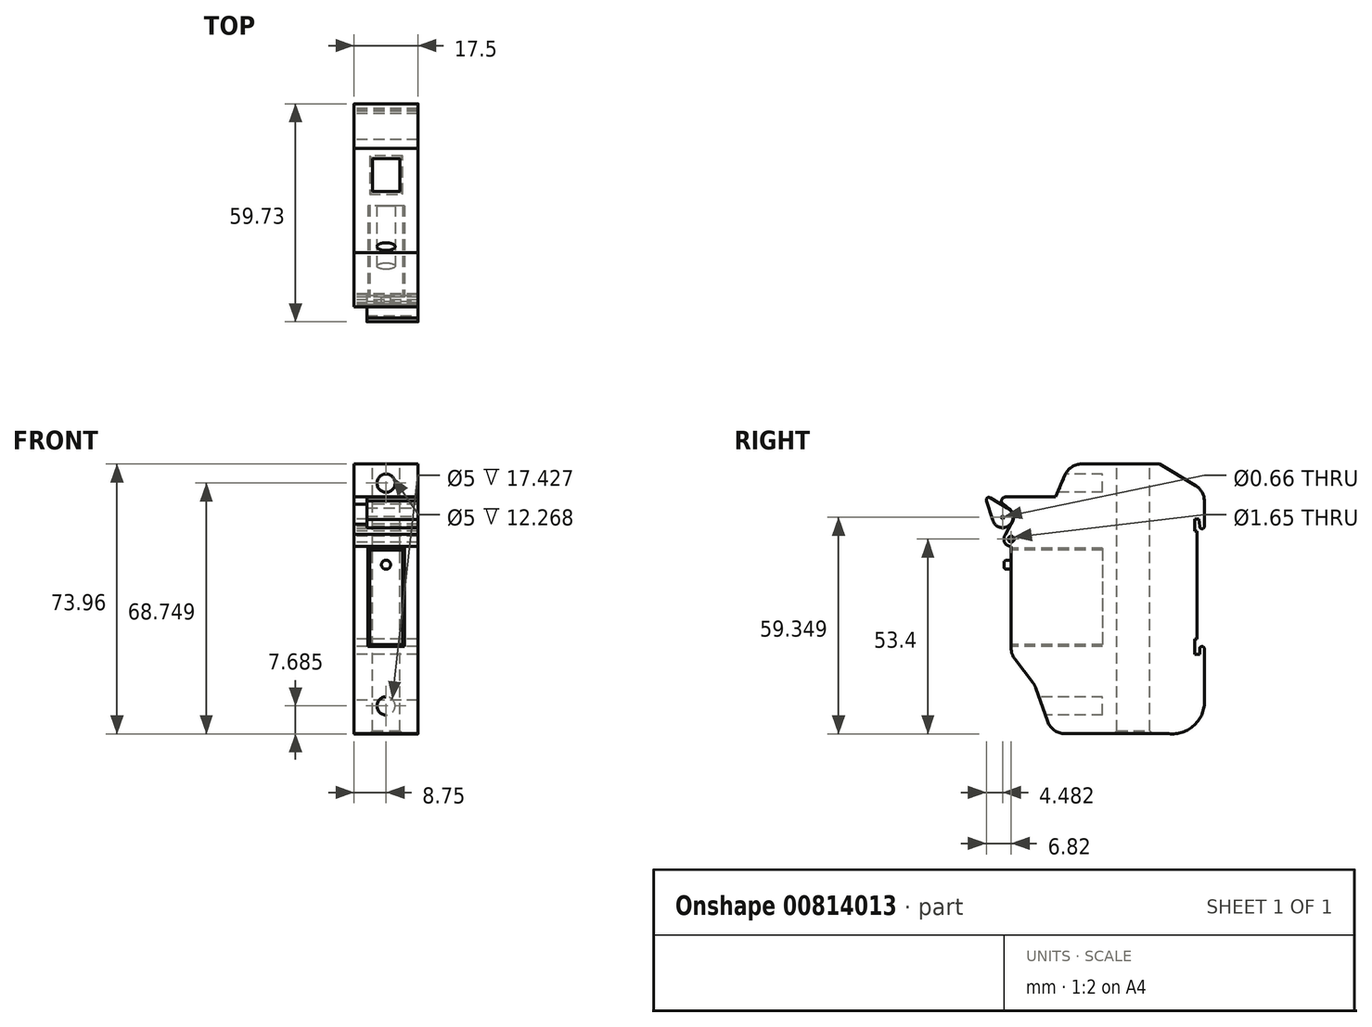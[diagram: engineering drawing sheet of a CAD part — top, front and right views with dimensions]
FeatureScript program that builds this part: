
annotation { "Feature Type Name" : "Feature", "Feature Type Description" : "" }
export const myFeature = defineFeature(function(context is Context, id is Id, definition is map)
    precondition{}
    {
        {
            var Q0;
            Q0=qCreatedBy(makeId("Right.planeOp"),FACE);
            var sketch = newSketch(context, id + "F0", { "sketchPlane" : qUnion([Q0])});
            skLineSegment(sketch, "E0", {"start": v(0, 86.45) * mm, "end": v(0, 33.6) * mm, "construction": true});
            skLineSegment(sketch, "E1", {"start": v(-101.47, 0) * mm, "end": v(113.77, 0) * mm, "construction": true});
            skLineSegment(sketch, "E2", {"start": v(0, 0) * mm, "end": v(0, -40.3) * mm});
            skLineSegment(sketch, "E3", {"start": v(14.7, -40.3) * mm, "end": v(45.1, -40.3) * mm});
            skLineSegment(sketch, "E4", {"start": v(52.9, -32.04) * mm, "end": v(52.9, -17.04) * mm});
            skLineSegment(sketch, "E5", {"start": v(40.66, 33.6) * mm, "end": v(19.3, 33.6) * mm});
            skLineSegment(sketch, "E6.bottom", {"start": v(51.37, 18.6) * mm, "end": v(50.3, 18.6) * mm});
            skLineSegment(sketch, "E6.top", {"start": v(52.9, -18.6) * mm, "end": v(50.3, -18.6) * mm});
            skLineSegment(sketch, "E6.right", {"start": v(50.3, 18.6) * mm, "end": v(50.3, 15.23) * mm});
            skPoint(sketch, "E6.middle", {"position": v(52.9, 0) * mm});
            skLineSegment(sketch, "E7", {"start": v(51.37, 18.6) * mm, "end": v(51.6, 16.51) * mm});
            skLineSegment(sketch, "E8.bottom", {"start": v(50.3, 15.23) * mm, "end": v(50.92, 15.23) * mm});
            skLineSegment(sketch, "E8.top", {"start": v(50.3, -14.35) * mm, "end": v(50.92, -14.35) * mm});
            skLineSegment(sketch, "E8.right", {"start": v(50.92, 15.23) * mm, "end": v(50.92, -14.35) * mm});
            skPoint(sketch, "E9.orphan", {"position": v(55.5, -18.6) * mm});
            skPoint(sketch, "E6.left.start.orphan", {"position": v(55.5, 18.6) * mm});
            skLineSegment(sketch, "E10.trimOffspring", {"start": v(52.9, 16.51) * mm, "end": v(52.9, 23.43) * mm});
            skLineSegment(sketch, "E11", {"start": v(51.6, -18.6) * mm, "end": v(51.6, -17.04) * mm});
            skLineSegment(sketch, "E12", {"start": v(52.9, -17.04) * mm, "end": v(52.9, -18.6) * mm});
            skArc(sketch, "E13", {"start": v(52.9, -17.04) * mm, "mid": v(52.25, -16.4) * mm, "end": v(51.6, -17.04) * mm});
            skArc(sketch, "E14", {"start": v(51.6, 16.51) * mm, "mid": v(52.25, 15.86) * mm, "end": v(52.9, 16.51) * mm});
            skLineSegment(sketch, "E15.trimOffspring", {"start": v(50.3, -14.35) * mm, "end": v(50.3, -18.6) * mm});
            skLineSegment(sketch, "E16", {"start": v(50.47, 27.72) * mm, "end": v(40.66, 33.6) * mm});
            skArc(sketch, "E17", {"start": v(43.12, -40.3) * mm, "mid": v(50.15, -37.96) * mm, "end": v(52.9, -31.07) * mm});
            skLineSegment(sketch, "E18.trimOffspring", {"start": v(0, -40.3) * mm, "end": v(0, -83.55) * mm, "construction": true});
            skLineSegment(sketch, "E19", {"start": v(9.98, -36.97) * mm, "end": v(6.69, -27.67) * mm});
            skLineSegment(sketch, "E20", {"start": v(5.93, -26.28) * mm, "end": v(1.04, -19.95) * mm});
            skLineSegment(sketch, "E21", {"start": v(0, 24.58) * mm, "end": v(12.18, 24.58) * mm});
            skLineSegment(sketch, "E22", {"start": v(12.18, 24.58) * mm, "end": v(14.7, 30.55) * mm});
            skArc(sketch, "E23", {"start": v(0, 17.15) * mm, "mid": v(0.61, 19.37) * mm, "end": v(-0.55, 21.36) * mm});
            skCircle(sketch, "E24", {"center": v(0, 13.04) * mm, "radius": 0.82 * mm});
            skArc(sketch, "E25", {"start": v(-1.54, 14.34) * mm, "mid": v(-1.83, 12.2) * mm, "end": v(0, 11.03) * mm});
            skLineSegment(sketch, "E26", {"start": v(-1.54, 14.34) * mm, "end": v(0.26, 17.53) * mm});
            skArc(sketch, "E27", {"start": v(-1.57, 24.58) * mm, "mid": v(-2.62, 23.78) * mm, "end": v(-2.13, 22.56) * mm});
            skLineSegment(sketch, "E28", {"start": v(0, 24.58) * mm, "end": v(-1.57, 24.58) * mm});
            skLineSegment(sketch, "E29", {"start": v(-2.13, 22.56) * mm, "end": v(-0.55, 21.36) * mm});
            skLineSegment(sketch, "E30.trimOffspring", {"start": v(0, 11.03) * mm, "end": v(0, -16.9) * mm, "construction": true});
            skLineSegment(sketch, "E31.trimOffspring", {"start": v(0, 11.03) * mm, "end": v(0, 0) * mm});
            skLineSegment(sketch, "E32.trimOffspring", {"start": v(0, 17.15) * mm, "end": v(0, 17.08) * mm, "construction": true});
            skLineSegment(sketch, "E33.trimOffspring", {"start": v(0, 17.15) * mm, "end": v(0, 17.08) * mm});
            skPoint(sketch, "E34.visualSharp", {"position": v(0, -18.6) * mm});
            skArc(sketch, "E34.filletArc", {"start": v(0, -16.9) * mm, "mid": v(0.27, -18.5) * mm, "end": v(1.04, -19.95) * mm});
            skPoint(sketch, "E35.visualSharp", {"position": v(6.42, -26.91) * mm});
            skArc(sketch, "E35.filletArc", {"start": v(6.69, -27.67) * mm, "mid": v(6.36, -26.94) * mm, "end": v(5.93, -26.28) * mm});
            skPoint(sketch, "E36.visualSharp", {"position": v(11.16, -40.3) * mm});
            skArc(sketch, "E36.filletArc", {"start": v(9.98, -36.97) * mm, "mid": v(11.8, -39.38) * mm, "end": v(14.7, -40.3) * mm});
            skPoint(sketch, "E37.visualSharp", {"position": v(15.99, 33.6) * mm});
            skArc(sketch, "E37.filletArc", {"start": v(19.3, 33.6) * mm, "mid": v(16.54, 32.77) * mm, "end": v(14.7, 30.55) * mm});
            skPoint(sketch, "E38.visualSharp", {"position": v(52.9, 26.27) * mm});
            skArc(sketch, "E38.filletArc", {"start": v(52.9, 23.43) * mm, "mid": v(52.25, 25.9) * mm, "end": v(50.47, 27.72) * mm});
            skSolve(sketch);
        }
        {
            var Q0;
            Q0=qSketchRegion(id+"F0",true);
            extrude(context, id + "F1", {"entities" : qUnion([Q0]), "depth" : 17.5 * mm, "offsetDistance" : 25 * mm});
        }
        {
            var Q0;
            Q0=makeQuery(id+"F1.opExtrude","CAP_FACE",FACE,{"disambiguationData":[OSD([sQuery(id+"F0.wireOp",EDGE,"E2"),sQuery(id+"F0.wireOp",EDGE,"E3"),sQuery(id+"F0.wireOp",EDGE,"E4"),sQuery(id+"F0.wireOp",EDGE,"E5"),sQuery(id+"F0.wireOp",EDGE,"E6.bottom"),sQuery(id+"F0.wireOp",EDGE,"E6.top"),sQuery(id+"F0.wireOp",EDGE,"E6.right"),sQuery(id+"F0.wireOp",EDGE,"E7"),sQuery(id+"F0.wireOp",EDGE,"E8.bottom"),sQuery(id+"F0.wireOp",EDGE,"E8.top"),sQuery(id+"F0.wireOp",EDGE,"E8.right"),sQuery(id+"F0.wireOp",EDGE,"E10.trimOffspring"),sQuery(id+"F0.wireOp",EDGE,"E11"),sQuery(id+"F0.wireOp",EDGE,"E12"),sQuery(id+"F0.wireOp",EDGE,"E13"),sQuery(id+"F0.wireOp",EDGE,"E14"),sQuery(id+"F0.wireOp",EDGE,"E15.trimOffspring"),sQuery(id+"F0.wireOp",EDGE,"E16"),sQuery(id+"F0.wireOp",EDGE,"E17"),sQuery(id+"F0.wireOp",EDGE,"E19"),sQuery(id+"F0.wireOp",EDGE,"E20"),sQuery(id+"F0.wireOp",EDGE,"E21"),sQuery(id+"F0.wireOp",EDGE,"E22"),sQuery(id+"F0.wireOp",EDGE,"E23"),sQuery(id+"F0.wireOp",EDGE,"E24"),sQuery(id+"F0.wireOp",EDGE,"E25"),sQuery(id+"F0.wireOp",EDGE,"E26"),sQuery(id+"F0.wireOp",EDGE,"E27"),sQuery(id+"F0.wireOp",EDGE,"E28"),sQuery(id+"F0.wireOp",EDGE,"E29"),sQuery(id+"F0.wireOp",EDGE,"E31.trimOffspring"),sQuery(id+"F0.wireOp",EDGE,"E33.trimOffspring"),sQuery(id+"F0.wireOp",EDGE,"E34.filletArc"),sQuery(id+"F0.wireOp",EDGE,"E35.filletArc"),sQuery(id+"F0.wireOp",EDGE,"E36.filletArc"),sQuery(id+"F0.wireOp",EDGE,"E37.filletArc"),sQuery(id+"F0.wireOp",EDGE,"E38.filletArc")])],"isStart":false});
            var sketch = newSketch(context, id + "F2", { "sketchPlane" : qUnion([Q0])});
            skArc(sketch, "E39", {"start": v(-5.1, 18.4) * mm, "mid": v(-0.56, 16.8) * mm, "end": v(-1.2, 21.57) * mm});
            skArc(sketch, "E40", {"start": v(-5.77, 24.34) * mm, "mid": v(-6.6, 24.31) * mm, "end": v(-6.73, 23.5) * mm});
            skLineSegment(sketch, "E41", {"start": v(-6.73, 23.5) * mm, "end": v(-4.92, 17.86) * mm});
            skLineSegment(sketch, "E42", {"start": v(-5.77, 24.34) * mm, "end": v(-1.2, 21.57) * mm});
            skCircle(sketch, "E43", {"center": v(-2.34, 18.99) * mm, "radius": 0.33 * mm});
            skSolve(sketch);
        }
        {
            var Q0;
            Q0=qSketchRegion(id+"F2",true);
            extrude(context, id + "F3", {"entities" : qUnion([Q0]), "oppositeDirection" : true, "depth" : 14 * mm, "offsetDistance" : 25 * mm});
        }
        {
            var Q0;
            Q0=makeQuery(id+"F1.opExtrude","SWEPT_FACE",FACE,{"disambiguationData":[OSD([sQuery(id+"F0.wireOp",EDGE,"E5")])]});
            var sketch = newSketch(context, id + "F4", { "sketchPlane" : qUnion([Q0])});
            skLineSegment(sketch, "E44.bottom", {"start": v(5, 37.9) * mm, "end": v(12.5, 37.9) * mm});
            skLineSegment(sketch, "E44.top", {"start": v(5, 28.9) * mm, "end": v(12.5, 28.9) * mm});
            skLineSegment(sketch, "E44.left", {"start": v(5, 37.9) * mm, "end": v(5, 28.9) * mm});
            skLineSegment(sketch, "E44.right", {"start": v(12.5, 37.9) * mm, "end": v(12.5, 28.9) * mm});
            skPoint(sketch, "E44.middle", {"position": v(8.75, 33.4) * mm});
            skPoint(sketch, "E44.middle.positionSnap0", {"position": v(8.75, 19.3) * mm});
            skPoint(sketch, "E44.centerSnap0", {"position": v(8.75, 19.3) * mm});
            skSolve(sketch);
        }
        {
            var Q0;
            Q0=qSketchRegion(id+"F4",true);
            extrude(context, id + "F5", {"entities" : qUnion([Q0]), "operationType" : NewBodyOperationType.REMOVE, "endBound" : BoundingType.THROUGH_ALL, "oppositeDirection" : true, "depth" : 25 * mm, "offsetDistance" : 25 * mm});
        }
        {
            var Q0;
            Q0=qCreatedBy(makeId("Front.planeOp"),FACE);
            var sketch = newSketch(context, id + "F6", { "sketchPlane" : qUnion([Q0])});
            skLineSegment(sketch, "E45", {"start": v(8.75, -59.1) * mm, "end": v(8.75, 50.81) * mm, "construction": true});
            skCircle(sketch, "E46", {"center": v(8.75, -32.68) * mm, "radius": 2.5 * mm});
            skCircle(sketch, "E47", {"center": v(8.75, 28.39) * mm, "radius": 2.5 * mm});
            skSolve(sketch);
        }
        {
            var Q0;
            Q0=qSketchRegion(id+"F6",true);
            extrude(context, id + "F7", {"entities" : qUnion([Q0]), "operationType" : NewBodyOperationType.REMOVE, "oppositeDirection" : true, "depth" : 25 * mm, "offsetDistance" : 25 * mm});
        }
        {
            var Q0;
            Q0=makeQuery(id+"F1.opExtrude","SWEPT_FACE",FACE,{"disambiguationData":[OSD([sQuery(id+"F0.wireOp",EDGE,"E2"),sQuery(id+"F0.wireOp",EDGE,"E31.trimOffspring")])]});
            var sketch = newSketch(context, id + "F8", { "sketchPlane" : qUnion([Q0])});
            skLineSegment(sketch, "E48.bottom", {"start": v(13.75, 10.57) * mm, "end": v(3.75, 10.57) * mm});
            skLineSegment(sketch, "E48.top", {"start": v(13.75, -16.43) * mm, "end": v(3.75, -16.43) * mm});
            skLineSegment(sketch, "E48.left", {"start": v(13.75, 10.57) * mm, "end": v(13.75, -16.43) * mm});
            skLineSegment(sketch, "E48.right", {"start": v(3.75, 10.57) * mm, "end": v(3.75, -16.43) * mm});
            skPoint(sketch, "E48.middle", {"position": v(8.75, -2.93) * mm});
            skPoint(sketch, "E48.middle.positionSnap0", {"position": v(17.5, -2.93) * mm});
            skPoint(sketch, "E48.middle.positionSnap1", {"position": v(8.75, -16.9) * mm});
            skPoint(sketch, "E48.centerSnap0", {"position": v(17.5, -2.93) * mm});
            skPoint(sketch, "E48.centerSnap1", {"position": v(8.75, -16.9) * mm});
            skLineSegment(sketch, "E49.bottom", {"start": v(13.25, 10.07) * mm, "end": v(4.25, 10.07) * mm});
            skLineSegment(sketch, "E49.top", {"start": v(13.25, -15.93) * mm, "end": v(4.25, -15.93) * mm});
            skLineSegment(sketch, "E49.left", {"start": v(13.25, 10.07) * mm, "end": v(13.25, -15.93) * mm});
            skLineSegment(sketch, "E49.right", {"start": v(4.25, 10.07) * mm, "end": v(4.25, -15.93) * mm});
            skSolve(sketch);
        }
        {
            var Q0;
            Q0=qSketchRegion(id+"F8",true);
            extrude(context, id + "F9", {"entities" : qUnion([Q0]), "operationType" : NewBodyOperationType.REMOVE, "oppositeDirection" : true, "depth" : 25 * mm, "offsetDistance" : 25 * mm});
        }
        {
            var Q0;
            Q0=makeQuery(id+"F9.boolean.opBoolean","SPLIT",FACE,{"disambiguationData":[TD([makeQuery(id+"F9.opExtrude","SWEPT_FACE",FACE,{"disambiguationData":[OSD([sQuery(id+"F8.wireOp",EDGE,"E49.bottom")])]})])],"derivedFrom":makeQuery(id+"F1.opExtrude","SWEPT_FACE",FACE,{"disambiguationData":[OSD([sQuery(id+"F0.wireOp",EDGE,"E2"),sQuery(id+"F0.wireOp",EDGE,"E31.trimOffspring")])]})});
            var sketch = newSketch(context, id + "F10", { "sketchPlane" : qUnion([Q0])});
            skCircle(sketch, "E50", {"center": v(8.75, 6.02) * mm, "radius": 1.25 * mm});
            skPoint(sketch, "E50.centerSnap0", {"position": v(8.75, 10.07) * mm});
            skSolve(sketch);
        }
        {
            var Q0;
            Q0=qSketchRegion(id+"F10",true);
            extrude(context, id + "F11", {"entities" : qUnion([Q0]), "operationType" : NewBodyOperationType.ADD, "depth" : 2 * mm, "offsetDistance" : 25 * mm});
        }
        {
            var Q0;
            Q0=makeQuery(id+"F11.opExtrude","CAP_EDGE",EDGE,{"disambiguationData":[OSD([sQuery(id+"F10.wireOp",EDGE,"E50")])],"isStart":false});
            fillet(context, id + "F12", {"entities" : qUnion([Q0]), "radius" : .75 * mm, "tangentPropagation" : true, "allowEdgeOverflow" : false});
        }
        {
            var Q0;
            Q0=makeQuery(id+"F5.boolean.opBoolean","INTERSECT",EDGE,{"derivedFrom":[makeQuery(id+"F1.opExtrude","SWEPT_FACE",FACE,{"disambiguationData":[OSD([sQuery(id+"F0.wireOp",EDGE,"E3")])]}),makeQuery(id+"F5.opExtrude","SWEPT_FACE",FACE,{"disambiguationData":[OSD([sQuery(id+"F4.wireOp",EDGE,"E44.bottom")])]})]});
            var Q1;
            Q1=makeQuery(id+"F5.boolean.opBoolean","INTERSECT",EDGE,{"derivedFrom":[makeQuery(id+"F1.opExtrude","SWEPT_FACE",FACE,{"disambiguationData":[OSD([sQuery(id+"F0.wireOp",EDGE,"E3")])]}),makeQuery(id+"F5.opExtrude","SWEPT_FACE",FACE,{"disambiguationData":[OSD([sQuery(id+"F4.wireOp",EDGE,"E44.right")])]})]});
            var Q2;
            Q2=makeQuery(id+"F5.boolean.opBoolean","INTERSECT",EDGE,{"derivedFrom":[makeQuery(id+"F1.opExtrude","SWEPT_FACE",FACE,{"disambiguationData":[OSD([sQuery(id+"F0.wireOp",EDGE,"E3")])]}),makeQuery(id+"F5.opExtrude","SWEPT_FACE",FACE,{"disambiguationData":[OSD([sQuery(id+"F4.wireOp",EDGE,"E44.top")])]})]});
            var Q3;
            Q3=makeQuery(id+"F5.boolean.opBoolean","INTERSECT",EDGE,{"derivedFrom":[makeQuery(id+"F1.opExtrude","SWEPT_FACE",FACE,{"disambiguationData":[OSD([sQuery(id+"F0.wireOp",EDGE,"E3")])]}),makeQuery(id+"F5.opExtrude","SWEPT_FACE",FACE,{"disambiguationData":[OSD([sQuery(id+"F4.wireOp",EDGE,"E44.left")])]})]});
            var Q4;
            Q4=makeQuery(id+"F5.boolean.opBoolean","COPY",EDGE,{"derivedFrom":makeQuery(id+"F5.opExtrude","CAP_EDGE",EDGE,{"disambiguationData":[OSD([sQuery(id+"F4.wireOp",EDGE,"E44.left")])],"isStart":true})});
            var Q5;
            Q5=makeQuery(id+"F5.boolean.opBoolean","COPY",EDGE,{"derivedFrom":makeQuery(id+"F5.opExtrude","CAP_EDGE",EDGE,{"disambiguationData":[OSD([sQuery(id+"F4.wireOp",EDGE,"E44.top")])],"isStart":true})});
            var Q6;
            Q6=makeQuery(id+"F5.boolean.opBoolean","COPY",EDGE,{"derivedFrom":makeQuery(id+"F5.opExtrude","CAP_EDGE",EDGE,{"disambiguationData":[OSD([sQuery(id+"F4.wireOp",EDGE,"E44.right")])],"isStart":true})});
            var Q7;
            Q7=makeQuery(id+"F5.boolean.opBoolean","COPY",EDGE,{"derivedFrom":makeQuery(id+"F5.opExtrude","CAP_EDGE",EDGE,{"disambiguationData":[OSD([sQuery(id+"F4.wireOp",EDGE,"E44.bottom")])],"isStart":true})});
            chamfer(context, id + "F13", {"entities" : qUnion([Q0, Q1, Q2, Q3, Q4, Q5, Q6, Q7]), "width" : .75 * mm, "tangentPropagation" : true});
        }
    });
